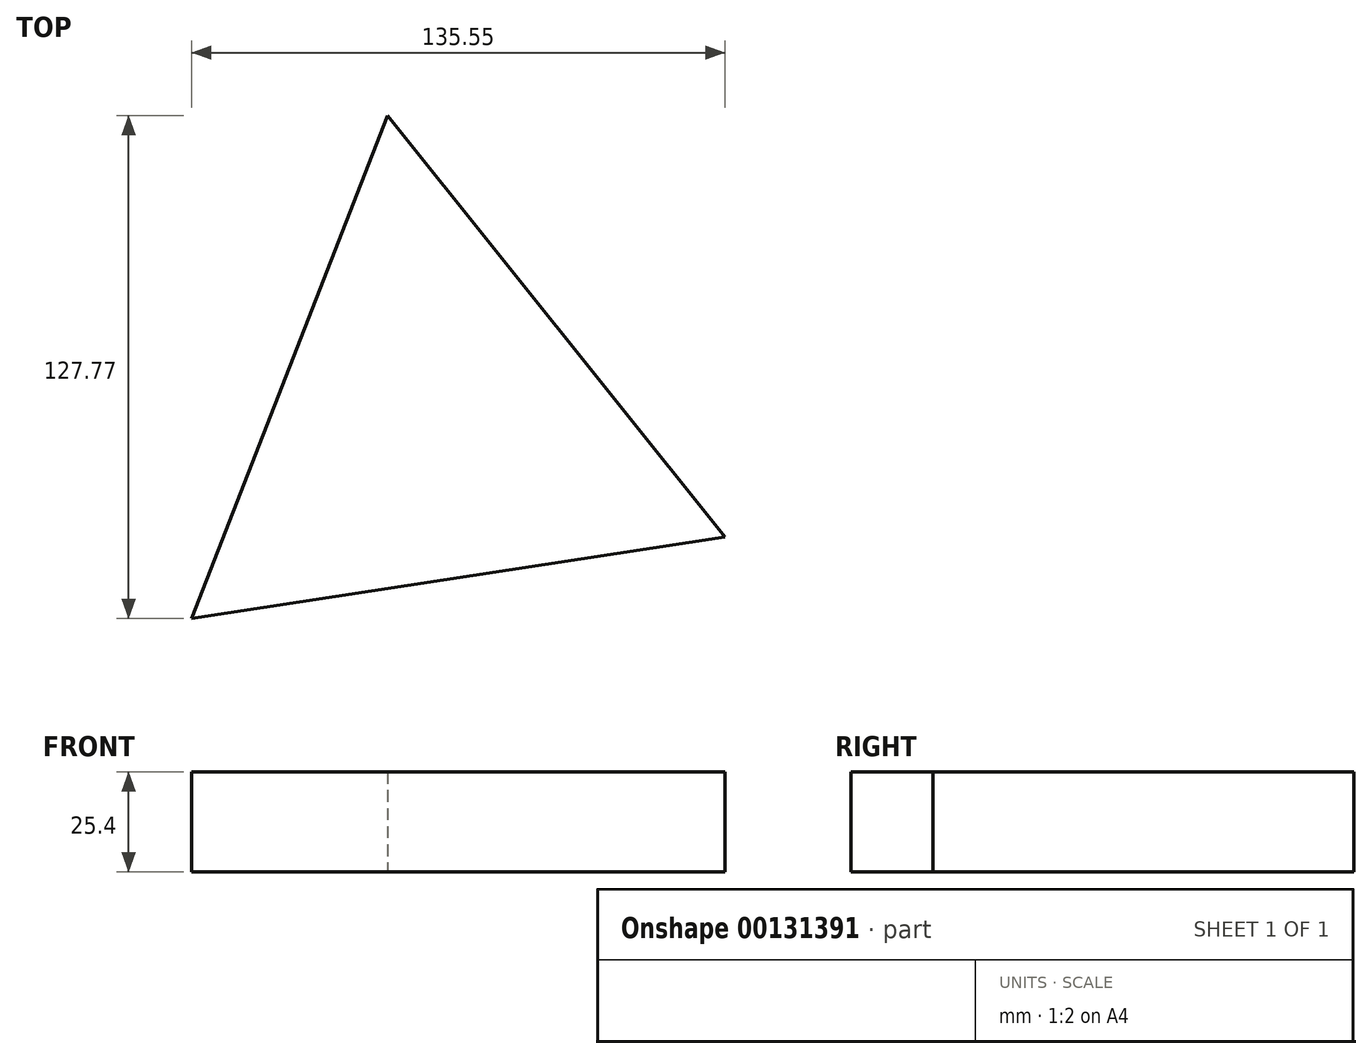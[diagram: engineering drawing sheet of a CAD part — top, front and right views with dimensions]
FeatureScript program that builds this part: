
annotation { "Feature Type Name" : "Feature", "Feature Type Description" : "" }
export const myFeature = defineFeature(function(context is Context, id is Id, definition is map)
    precondition{}
    {
        {
            var Q0;
            Q0=qCreatedBy(makeId("Top.planeOp"),FACE);
            var sketch = newSketch(context, id + "F0", { "sketchPlane" : qUnion([Q0])});
            skCircle(sketch, "E0.cCircle", {"center": v(0, 0) * mm, "radius": 39.59 * mm, "construction": true});
            skLineSegment(sketch, "E0.0", {"start": v(-61.78, -49.5) * mm, "end": v(-11.98, 78.26) * mm});
            skLineSegment(sketch, "E0.1", {"start": v(-11.98, 78.26) * mm, "end": v(73.77, -28.75) * mm});
            skLineSegment(sketch, "E0.2", {"start": v(73.77, -28.75) * mm, "end": v(-61.78, -49.5) * mm});
            skPoint(sketch, "E0.0.midPoint", {"position": v(-36.88, 14.38) * mm});
            skSolve(sketch);
        }
        {
            var Q0;
            Q0=makeQuery(id+"F0.imprint","IMPRINT",FACE,{"disambiguationData":[TD([[makeQuery(id+"F0.imprint","IMPRINT",EDGE,{"derivedFrom":sQuery(id+"F0.wireOp",EDGE,"E0.0")}),-1.0]])]});
            var Q1;
            Q1 = qSketchRegion(id + "F0", true);
            extrude(context, id + "F1", {"entities" : qUnion([Q0, Q1]), "depth" : 25.4 * mm});
        }
    });
